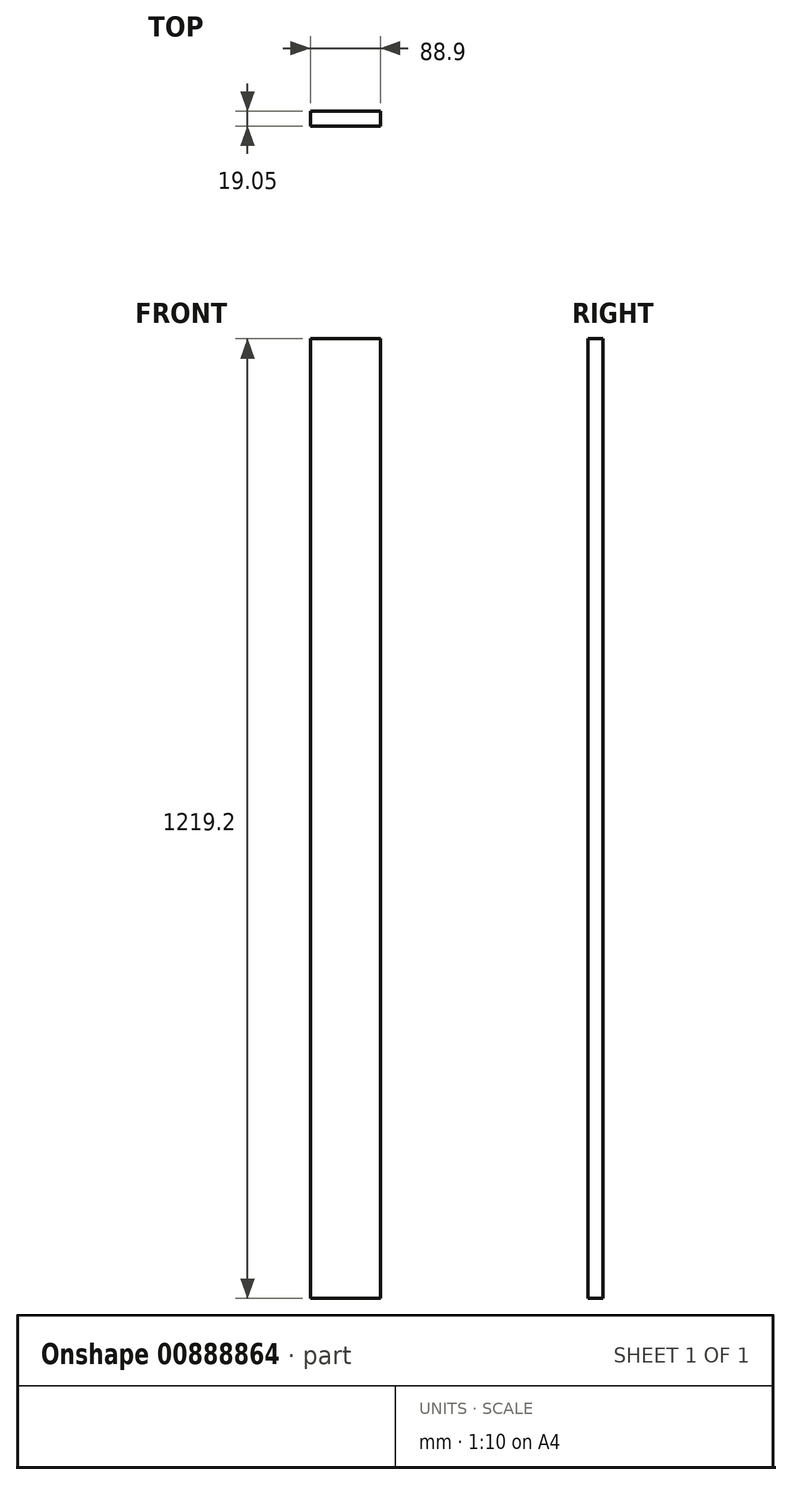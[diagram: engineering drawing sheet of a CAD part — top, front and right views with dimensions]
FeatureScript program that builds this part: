
annotation { "Feature Type Name" : "Feature", "Feature Type Description" : "" }
export const myFeature = defineFeature(function(context is Context, id is Id, definition is map)
    precondition{}
    {
        {
            var Q0;
            Q0=qCreatedBy(makeId("Front.planeOp"),FACE);
            var sketch = newSketch(context, id + "F0", { "sketchPlane" : qUnion([Q0])});
            skLineSegment(sketch, "E0.bottom", {"start": v(0, 0) * mm, "end": v(-88.9, 0) * mm});
            skLineSegment(sketch, "E0.top", {"start": v(0, 1219.2) * mm, "end": v(-88.9, 1219.2) * mm});
            skLineSegment(sketch, "E0.left", {"start": v(0, 0) * mm, "end": v(0, 1219.2) * mm});
            skLineSegment(sketch, "E0.right", {"start": v(-88.9, 0) * mm, "end": v(-88.9, 1219.2) * mm});
            skSolve(sketch);
        }
        {
            var Q0;
            Q0 = qSketchRegion(id + "F0", true);
            extrude(context, id + "F1", {"entities" : qUnion([Q0]), "depth" : 19.05 * mm, "offsetDistance" : 25.4 * mm});
        }
    });
